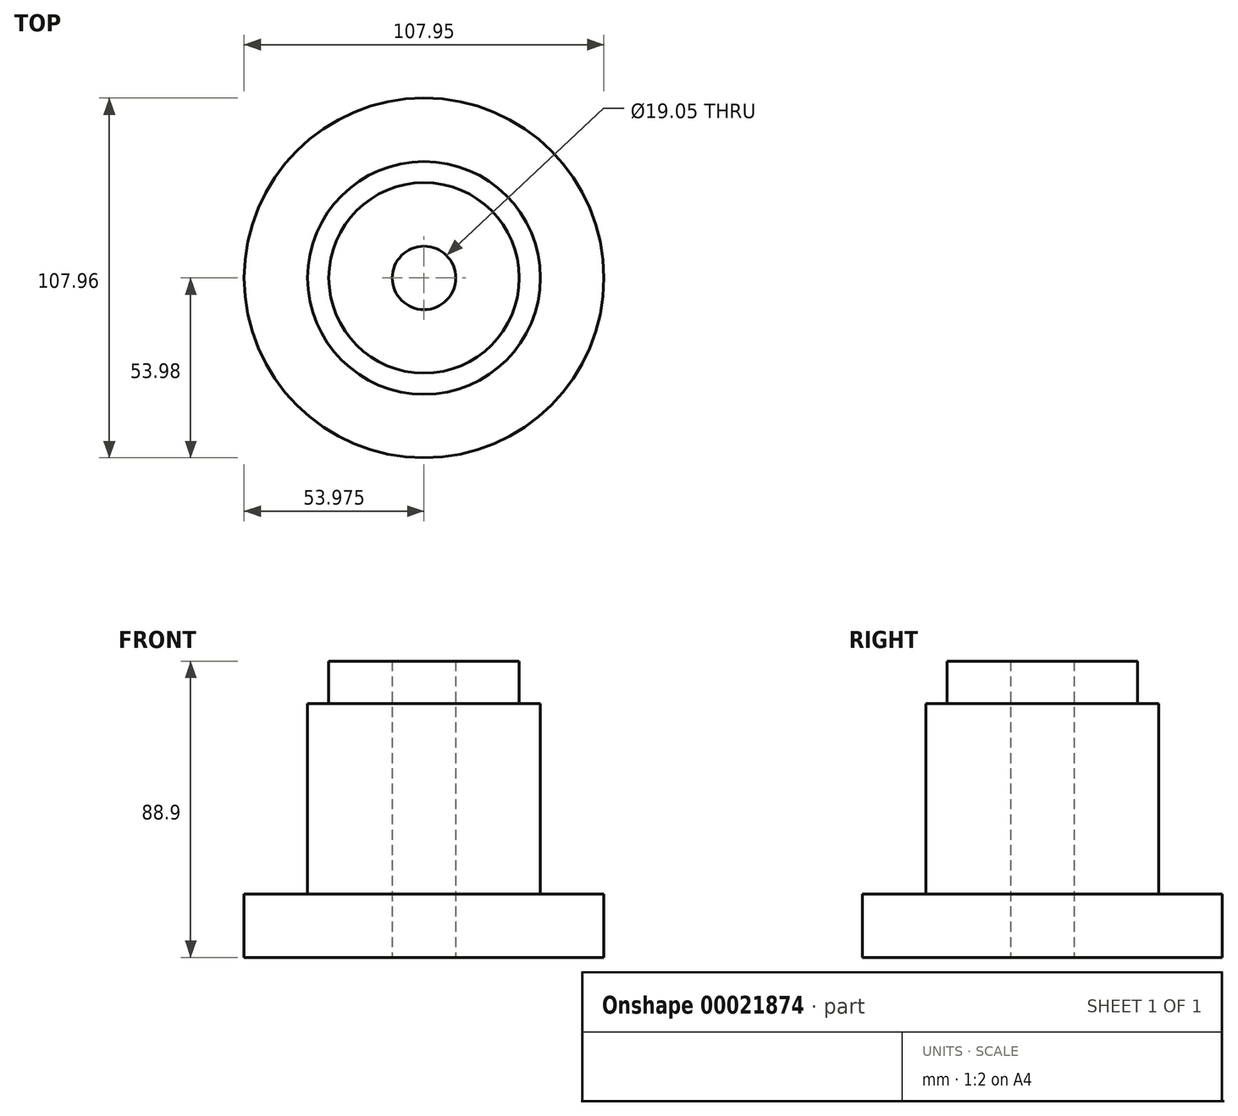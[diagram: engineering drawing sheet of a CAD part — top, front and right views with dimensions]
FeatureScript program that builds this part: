
annotation { "Feature Type Name" : "Feature", "Feature Type Description" : "" }
export const myFeature = defineFeature(function(context is Context, id is Id, definition is map)
    precondition{}
    {
        {
            var Q0;
            Q0=qCreatedBy(makeId("Front.planeOp"),FACE);
            var sketch = newSketch(context, id + "F0", { "sketchPlane" : qUnion([Q0])});
            skLineSegment(sketch, "E0", {"start": v(19.05, 67.52) * mm, "end": v(19.05, 54.82) * mm});
            skLineSegment(sketch, "E1", {"start": v(19.05, 54.82) * mm, "end": v(25.4, 54.82) * mm});
            skLineSegment(sketch, "E2", {"start": v(25.4, 54.82) * mm, "end": v(25.4, -2.33) * mm});
            skLineSegment(sketch, "E3", {"start": v(25.4, -2.33) * mm, "end": v(44.45, -2.33) * mm});
            skLineSegment(sketch, "E4", {"start": v(44.45, -2.33) * mm, "end": v(44.45, -21.38) * mm});
            skLineSegment(sketch, "E5", {"start": v(44.45, -21.38) * mm, "end": v(0, -21.38) * mm});
            skLineSegment(sketch, "E6", {"start": v(-10.43, 67.52) * mm, "end": v(-10.43, 66.61) * mm});
            skPoint(sketch, "E7.orphan", {"position": v(-10.43, -21.38) * mm});
            skLineSegment(sketch, "E8", {"start": v(19.05, 67.52) * mm, "end": v(0, 67.52) * mm});
            skLineSegment(sketch, "E9", {"start": v(0, 67.52) * mm, "end": v(0, -21.38) * mm});
            skLineSegment(sketch, "E10", {"start": v(-9.52, -21.38) * mm, "end": v(-9.52, 67.52) * mm});
            skSolve(sketch);
        }
        {
            var Q0;
            Q0=makeQuery(id+"F0.imprint","IMPRINT",FACE,{"disambiguationData":[TD([[makeQuery(id+"F0.imprint","IMPRINT",EDGE,{"derivedFrom":sQuery(id+"F0.wireOp",EDGE,"E0")}),-1.0]])]});
            var Q1;
            Q1=sQuery(id+"F0.wireOp",EDGE,"E10");
            revolve(context, id + "F1", {"entities" : qUnion([Q0]), "axis" : qUnion([Q1]), "revolveType" : RevolveType.FULL});
        }
    });
